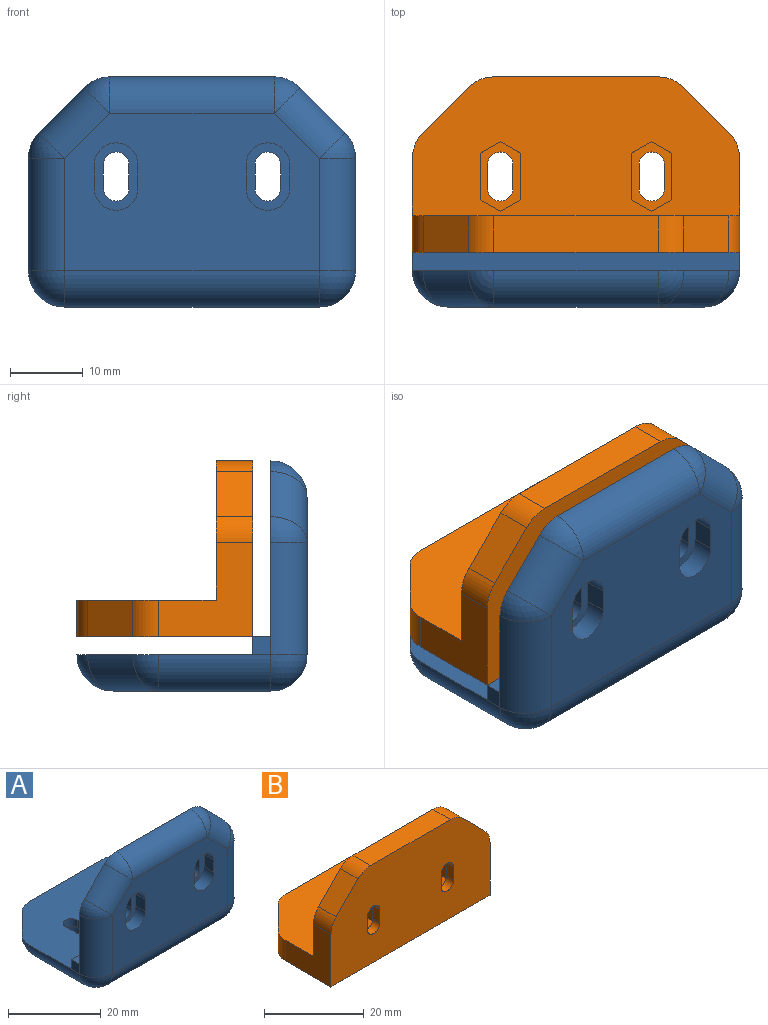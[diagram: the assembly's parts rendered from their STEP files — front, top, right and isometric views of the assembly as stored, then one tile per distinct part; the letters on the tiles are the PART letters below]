
ASSEMBLY  parts=2 mates=1
PART A: 65 faces, bbox 45x31.6x31.6 mm
  f0: plane 45x24.14mm, normal (0,0,1), area 958.7mm2, adj f1,f2,f3,f4,f5,f6,f7,f8
  f1: cylinder r=1.75mm len=3.5mm, axis (0,0,-1), area 11mm2, adj f0,f2,f8,f22
  f2: plane 3.25x2mm, normal (-1,0,0), area 6.5mm2, adj f0,f1,f3,f22
  f3: cylinder r=1.75mm len=3.5mm, axis (0,0,-1), area 11mm2, adj f0,f2,f8,f22
  f4: cylinder r=1.75mm len=3.5mm, axis (0,0,-1), area 11mm2, adj f0,f5,f7,f17
  f5: plane 3.25x2mm, normal (-1,0,0), area 6.5mm2, adj f0,f4,f6,f17
  f6: cylinder r=1.75mm len=3.5mm, axis (0,0,-1), area 11mm2, adj f0,f5,f7,f17
  f7: plane 3.25x2mm, normal (1,0,0), area 6.5mm2, adj f0,f4,f6,f17
  f8: plane 3.25x2mm, normal (1,0,0), area 6.5mm2, adj f0,f1,f3,f22
  f9: plane 35x21.64mm, normal (0,0,-1), area 623.3mm2, adj f13,f14,f15,f16,f18,f19,f20,f21
  f10: plane 2.5x2.5mm, normal (1,0,0), area 6.2mm2, adj f42,f43,f51,f52
  f11: plane 2.5x2.5mm, normal (-1,0,0), area 6.2mm2, adj f42,f43,f59,f63
  f12: plane 35x21.64mm, normal (0,-1,0), area 623.3mm2, adj f32,f33,f34,f35,f37,f38,f39,f40
  f13: plane 3.25x3mm, normal (-1,0,0), area 9.7mm2, adj f9,f14,f16,f17
  f14: cylinder r=3mm len=6mm, axis (0,0,-1), area 28.3mm2, adj f9,f13,f15,f17
  f15: plane 3.25x3mm, normal (1,0,0), area 9.7mm2, adj f9,f14,f16,f17
  f16: cylinder r=3mm len=6mm, axis (0,0,-1), area 28.3mm2, adj f9,f13,f15,f17
  f17: plane 9.25x6mm, normal (0,0,-1), area 26.8mm2, adj f4,f5,f6,f7,f13,f14,f15,f16
  f18: cylinder r=3mm len=6mm, axis (0,0,-1), area 28.3mm2, adj f9,f19,f21,f22
  f19: plane 3.25x3mm, normal (1,0,0), area 9.7mm2, adj f9,f18,f20,f22
  f20: cylinder r=3mm len=6mm, axis (0,0,-1), area 28.3mm2, adj f9,f19,f21,f22
  f21: plane 3.25x3mm, normal (-1,0,0), area 9.7mm2, adj f9,f18,f20,f22
  f22: plane 9.25x6mm, normal (0,0,-1), area 26.8mm2, adj f1,f2,f3,f8,f18,f19,f20,f21
  f23: cylinder r=1.75mm len=3.5mm, axis (0,-1,0), area 11mm2, adj f24,f30,f31,f41
  f24: plane 3.25x2mm, normal (-1,0,0), area 6.5mm2, adj f23,f25,f31,f41
  f25: cylinder r=1.75mm len=3.5mm, axis (0,-1,0), area 11mm2, adj f24,f30,f31,f41
  f26: cylinder r=1.75mm len=3.5mm, axis (0,-1,0), area 11mm2, adj f27,f29,f31,f36
  f27: plane 3.25x2mm, normal (-1,0,0), area 6.5mm2, adj f26,f28,f31,f36
  f28: cylinder r=1.75mm len=3.5mm, axis (0,-1,0), area 11mm2, adj f27,f29,f31,f36
  f29: plane 3.25x2mm, normal (1,0,0), area 6.5mm2, adj f26,f28,f31,f36
  f30: plane 3.25x2mm, normal (1,0,0), area 6.5mm2, adj f23,f25,f31,f41
  f31: plane 45x24.14mm, normal (0,1,0), area 958.7mm2, adj f23,f24,f25,f26,f27,f28,f29,f30
  f32: plane 3.25x3mm, normal (-1,0,0), area 9.7mm2, adj f12,f33,f35,f36
  f33: cylinder r=3mm len=6mm, axis (0,-1,0), area 28.3mm2, adj f12,f32,f34,f36
  f34: plane 3.25x3mm, normal (1,0,0), area 9.7mm2, adj f12,f33,f35,f36
  f35: cylinder r=3mm len=6mm, axis (0,-1,0), area 28.3mm2, adj f12,f32,f34,f36
  f36: plane 9.25x6mm, normal (0,-1,0), area 26.8mm2, adj f26,f27,f28,f29,f32,f33,f34,f35
  f37: cylinder r=3mm len=6mm, axis (0,-1,0), area 28.3mm2, adj f12,f38,f40,f41
  f38: plane 3.25x3mm, normal (1,0,0), area 9.7mm2, adj f12,f37,f39,f41
  f39: cylinder r=3mm len=6mm, axis (0,-1,0), area 28.3mm2, adj f12,f38,f40,f41
  f40: plane 3.25x3mm, normal (-1,0,0), area 9.7mm2, adj f12,f37,f39,f41
  f41: plane 9.25x6mm, normal (0,-1,0), area 26.8mm2, adj f23,f24,f25,f30,f37,f38,f39,f40
  f42: plane 45x2.5mm, normal (0,0,1), area 112.5mm2, adj f10,f11,f31,f43
  f43: plane 45x2.5mm, normal (0,1,0), area 112.5mm2, adj f0,f10,f11,f42
  f44: sphere r=5mm, area 19.6mm2, adj f0,f45,f46
  f45: cylinder r=5mm len=9.75mm, axis (-0.71,0.71,0), area 69mm2, adj f0,f9,f44,f48
  f46: cylinder r=5mm len=22.57mm, axis (-1,0,0), area 177.3mm2, adj f0,f9,f44,f49
  f47: sphere r=5mm, area 19.6mm2, adj f31,f50,f51
  f48: sphere r=5mm, area 19.6mm2, adj f0,f45,f52
  f49: sphere r=5mm, area 19.6mm2, adj f0,f46,f53
  f50: cylinder r=5mm len=9.75mm, axis (-0.71,0,0.71), area 69mm2, adj f12,f31,f47,f54
  f51: cylinder r=5mm len=15.43mm, axis (0,0,-1), area 121.2mm2, adj f10,f12,f31,f47,f55
  f52: cylinder r=5mm len=15.43mm, axis (0,1,0), area 121.2mm2, adj f0,f9,f10,f48,f55
  f53: cylinder r=5mm len=9.75mm, axis (-0.71,-0.71,0), area 69mm2, adj f0,f9,f49,f56
  f54: sphere r=5mm, area 19.6mm2, adj f31,f50,f57
  f55: sphere r=5mm, area 39.3mm2, adj f51,f52,f58
  f56: sphere r=5mm, area 19.6mm2, adj f0,f53,f59
  f57: cylinder r=5mm len=22.57mm, axis (-1,0,0), area 177.3mm2, adj f12,f31,f54,f60
  f58: cylinder r=5mm len=35mm, axis (1,0,0), area 274.9mm2, adj f9,f12,f55,f61
  f59: cylinder r=5mm len=15.43mm, axis (0,-1,0), area 121.2mm2, adj f0,f9,f11,f56,f61
  f60: sphere r=5mm, area 19.6mm2, adj f31,f57,f62
  f61: sphere r=5mm, area 39.3mm2, adj f58,f59,f63
  f62: cylinder r=5mm len=9.75mm, axis (-0.71,0,-0.71), area 69mm2, adj f12,f31,f60,f64
  f63: cylinder r=5mm len=15.43mm, axis (0,0,1), area 121.2mm2, adj f11,f12,f31,f61,f64
  f64: sphere r=5mm, area 19.6mm2, adj f31,f62,f63
PART B: 64 faces, bbox 45x24.1x24.1 mm
  f0: plane 9.6x5.5mm, normal (0,0,1), area 23.1mm2, adj f10,f11,f12,f14,f22,f23,f24,f25
  f1: plane 9.6x5.5mm, normal (0,0,1), area 23.1mm2, adj f7,f8,f9,f13,f17,f18,f19,f20
  f2: plane 45x24.14mm, normal (0,-1,0), area 958.7mm2, adj f3,f15,f16,f32,f33,f34,f35,f36
  f3: plane 12.93x12.93mm, normal (1,0,0), area 104.3mm2, adj f2,f16,f29,f55,f56,f60
  f4: plane 6.21x6.21mm, normal (0.71,0.71,0), area 43.9mm2, adj f16,f29,f60,f61
  f5: plane 22.57x5mm, normal (0,1,0), area 112.9mm2, adj f16,f29,f61,f62
  f6: plane 6.21x6.21mm, normal (-0.71,0.71,0), area 43.9mm2, adj f16,f29,f62,f63
  f7: cylinder r=1.75mm len=3.5mm, axis (0,0,-1), area 11mm2, adj f1,f8,f13,f16
  f8: plane 3.25x2mm, normal (-1,0,0), area 6.5mm2, adj f1,f7,f9,f16
  f9: cylinder r=1.75mm len=3.5mm, axis (0,0,-1), area 11mm2, adj f1,f8,f13,f16
  f10: cylinder r=1.75mm len=3.5mm, axis (0,0,-1), area 11mm2, adj f0,f11,f14,f16
  f11: plane 3.25x2mm, normal (-1,0,0), area 6.5mm2, adj f0,f10,f12,f16
  f12: cylinder r=1.75mm len=3.5mm, axis (0,0,-1), area 11mm2, adj f0,f11,f14,f16
  f13: plane 3.25x2mm, normal (1,0,0), area 6.5mm2, adj f1,f7,f9,f16
  f14: plane 3.25x2mm, normal (1,0,0), area 6.5mm2, adj f0,f10,f12,f16
  f15: plane 12.93x12.93mm, normal (-1,0,0), area 104.3mm2, adj f2,f16,f29,f55,f59,f63
  f16: plane 45x24.14mm, normal (0,0,-1), area 958.7mm2, adj f2,f3,f4,f5,f6,f7,f8,f9
  f17: plane 6.43x3mm, normal (-1,0,0), area 19.3mm2, adj f1,f18,f27,f29
  f18: plane 3x2.75mm, normal (-0.5,0.87,0), area 9.5mm2, adj f1,f17,f19,f29
  f19: plane 3x2.75mm, normal (0.5,0.87,0), area 9.5mm2, adj f1,f18,f20,f29
  f20: plane 6.43x3mm, normal (1,0,0), area 19.3mm2, adj f1,f19,f21,f29
  f21: plane 3x2.75mm, normal (0.5,-0.87,0), area 9.5mm2, adj f1,f20,f27,f29
  f22: plane 6.43x3mm, normal (-1,0,0), area 19.3mm2, adj f0,f23,f28,f29
  f23: plane 3x2.75mm, normal (-0.5,0.87,0), area 9.5mm2, adj f0,f22,f24,f29
  f24: plane 3x2.75mm, normal (0.5,0.87,0), area 9.5mm2, adj f0,f23,f25,f29
  f25: plane 6.43x3mm, normal (1,0,0), area 19.3mm2, adj f0,f24,f26,f29
  f26: plane 3x2.75mm, normal (0.5,-0.87,0), area 9.5mm2, adj f0,f25,f28,f29
  f27: plane 3x2.75mm, normal (-0.5,-0.87,0), area 9.5mm2, adj f1,f17,f21,f29
  f28: plane 3x2.75mm, normal (-0.5,-0.87,0), area 9.5mm2, adj f0,f22,f26,f29
  f29: plane 45x19.14mm, normal (0,0,1), area 687.5mm2, adj f3,f4,f5,f6,f15,f17,f18,f19
  f30: plane 9.6x5.5mm, normal (0,1,0), area 23.1mm2, adj f38,f39,f40,f42,f48,f49,f50,f51
  f31: plane 9.6x5.5mm, normal (0,1,0), area 23.1mm2, adj f35,f36,f37,f41,f43,f44,f45,f46
  f32: plane 6.21x6.21mm, normal (0.71,0,0.71), area 43.9mm2, adj f2,f55,f56,f57
  f33: plane 22.57x5mm, normal (0,0,1), area 112.9mm2, adj f2,f55,f57,f58
  f34: plane 6.21x6.21mm, normal (-0.71,0,0.71), area 43.9mm2, adj f2,f55,f58,f59
  f35: cylinder r=1.75mm len=3.5mm, axis (0,-1,0), area 11mm2, adj f2,f31,f36,f41
  f36: plane 3.25x2mm, normal (-1,0,0), area 6.5mm2, adj f2,f31,f35,f37
  f37: cylinder r=1.75mm len=3.5mm, axis (0,-1,0), area 11mm2, adj f2,f31,f36,f41
  f38: cylinder r=1.75mm len=3.5mm, axis (0,-1,0), area 11mm2, adj f2,f30,f39,f42
  f39: plane 3.25x2mm, normal (-1,0,0), area 6.5mm2, adj f2,f30,f38,f40
  f40: cylinder r=1.75mm len=3.5mm, axis (0,-1,0), area 11mm2, adj f2,f30,f39,f42
  f41: plane 3.25x2mm, normal (1,0,0), area 6.5mm2, adj f2,f31,f35,f37
  f42: plane 3.25x2mm, normal (1,0,0), area 6.5mm2, adj f2,f30,f38,f40
  f43: plane 6.43x3mm, normal (-1,0,0), area 19.3mm2, adj f31,f44,f53,f55
  f44: plane 3x2.75mm, normal (-0.5,0,0.87), area 9.5mm2, adj f31,f43,f45,f55
  f45: plane 3x2.75mm, normal (0.5,0,0.87), area 9.5mm2, adj f31,f44,f46,f55
  f46: plane 6.43x3mm, normal (1,0,0), area 19.3mm2, adj f31,f45,f47,f55
  f47: plane 3x2.75mm, normal (0.5,0,-0.87), area 9.5mm2, adj f31,f46,f53,f55
  f48: plane 6.43x3mm, normal (-1,0,0), area 19.3mm2, adj f30,f49,f54,f55
  f49: plane 3x2.75mm, normal (-0.5,0,0.87), area 9.5mm2, adj f30,f48,f50,f55
  f50: plane 3x2.75mm, normal (0.5,0,0.87), area 9.5mm2, adj f30,f49,f51,f55
  f51: plane 6.43x3mm, normal (1,0,0), area 19.3mm2, adj f30,f50,f52,f55
  f52: plane 3x2.75mm, normal (0.5,0,-0.87), area 9.5mm2, adj f30,f51,f54,f55
  f53: plane 3x2.75mm, normal (-0.5,0,-0.87), area 9.5mm2, adj f31,f43,f47,f55
  f54: plane 3x2.75mm, normal (-0.5,0,-0.87), area 9.5mm2, adj f30,f48,f52,f55
  f55: plane 45x19.14mm, normal (0,1,0), area 687.5mm2, adj f3,f15,f29,f32,f33,f34,f43,f44
  f56: cylinder r=5mm len=5mm, axis (0,-1,0), area 19.6mm2, adj f2,f3,f32,f55
  f57: cylinder r=5mm len=5mm, axis (0,-1,0), area 19.6mm2, adj f2,f32,f33,f55
  f58: cylinder r=5mm len=5mm, axis (0,-1,0), area 19.6mm2, adj f2,f33,f34,f55
  f59: cylinder r=5mm len=5mm, axis (0,-1,0), area 19.6mm2, adj f2,f15,f34,f55
  f60: cylinder r=5mm len=5mm, axis (0,0,-1), area 19.6mm2, adj f3,f4,f16,f29
  f61: cylinder r=5mm len=5mm, axis (0,0,-1), area 19.6mm2, adj f4,f5,f16,f29
  f62: cylinder r=5mm len=5mm, axis (0,0,-1), area 19.6mm2, adj f5,f6,f16,f29
  f63: cylinder r=5mm len=5mm, axis (0,0,-1), area 19.6mm2, adj f6,f15,f16,f29
PLACE A t=(-16.82,-11.45,-14.18)mm
PLACE B t=(-16.82,-3.95,-6.68)mm
MATE fastened B.f16 <-> A.f42  axis (0,0,-1) through (5.68,-3.95,-6.68)mm
